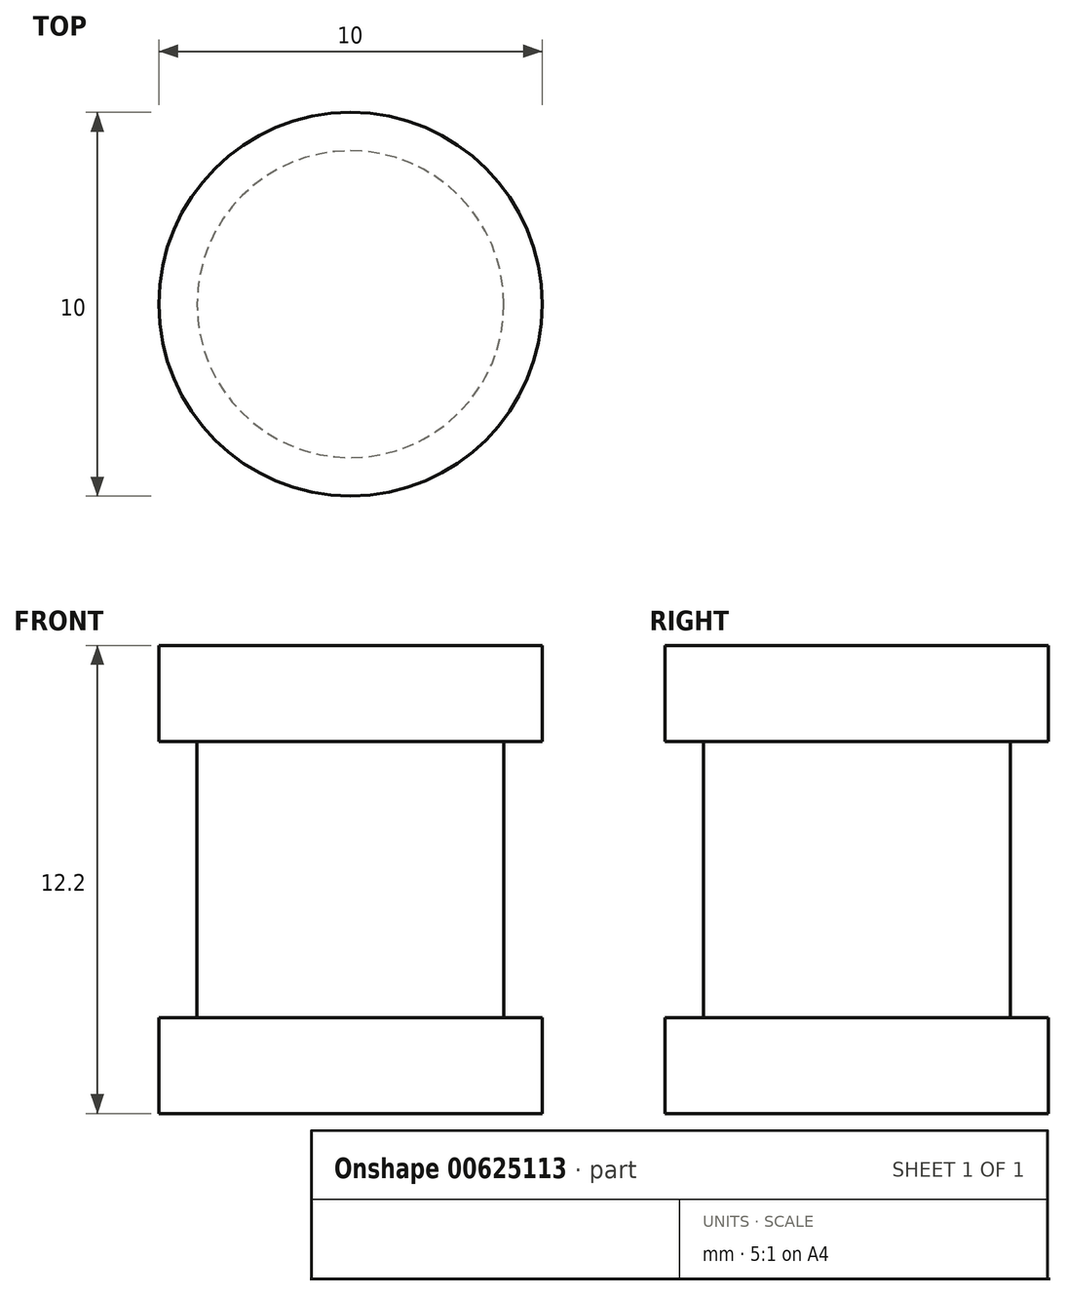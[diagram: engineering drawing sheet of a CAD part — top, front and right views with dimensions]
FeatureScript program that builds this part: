
annotation { "Feature Type Name" : "Feature", "Feature Type Description" : "" }
export const myFeature = defineFeature(function(context is Context, id is Id, definition is map)
    precondition{}
    {
        {
            var Q0;
            Q0=qCreatedBy(makeId("Top.planeOp"),FACE);
            var sketch = newSketch(context, id + "F0", { "sketchPlane" : qUnion([Q0])});
            skCircle(sketch, "E0", {"center": v(0, 0) * mm, "radius": 5 * mm});
            skSolve(sketch);
        }
        {
            var Q0;
            Q0=makeQuery(id+"F0.imprint","IMPRINT",FACE,{"disambiguationData":[TD([[makeQuery(id+"F0.imprint","IMPRINT",EDGE,{"derivedFrom":sQuery(id+"F0.wireOp",EDGE,"E0")}),1.0]])]});
            extrude(context, id + "F1", {"entities" : qUnion([Q0]), "depth" : 2.5 * mm, "offsetDistance" : 25 * mm});
        }
        {
            var Q0;
            Q0=makeQuery(id+"F1.opExtrude","CAP_FACE",FACE,{"disambiguationData":[OSD([sQuery(id+"F0.wireOp",EDGE,"E0")])],"isStart":false});
            var sketch = newSketch(context, id + "F2", { "sketchPlane" : qUnion([Q0])});
            skCircle(sketch, "E1", {"center": v(0, 0) * mm, "radius": 4 * mm});
            skSolve(sketch);
        }
        {
            var Q0;
            Q0=makeQuery(id+"F2.imprint","IMPRINT",FACE,{"disambiguationData":[TD([[makeQuery(id+"F2.imprint","IMPRINT",EDGE,{"derivedFrom":sQuery(id+"F2.wireOp",EDGE,"E1")}),1.0]])]});
            extrude(context, id + "F3", {"entities" : qUnion([Q0]), "operationType" : NewBodyOperationType.ADD, "depth" : 3.6 * mm, "offsetDistance" : 25 * mm});
        }
        {
            var Q0;
            Q0=makeQuery(id+"F3.opExtrude","CAP_FACE",FACE,{"disambiguationData":[OSD([sQuery(id+"F2.wireOp",EDGE,"E1")])],"isStart":false});
            cPlane(context, id + "F4", {"entities" : qUnion([Q0]), "cplaneType" : CPlaneType.OFFSET, "offset" : 0 * mm, "width" : 150 * mm, "height" : 150 * mm});
        }
        {
            var Q0;
            Q0=makeQuery(id+"F1.opExtrude","SWEPT_BODY",BODY,{"disambiguationData":[OSD([sQuery(id+"F0.wireOp",EDGE,"E0")])]});
            var Q1;
            Q1=qCreatedBy(id+"F4.planeOp",FACE);
            mirror(context, id + "F5", {"operationType" : NewBodyOperationType.ADD, "entities" : qUnion([Q0]), "mirrorPlane" : qUnion([Q1])});
        }
    });
